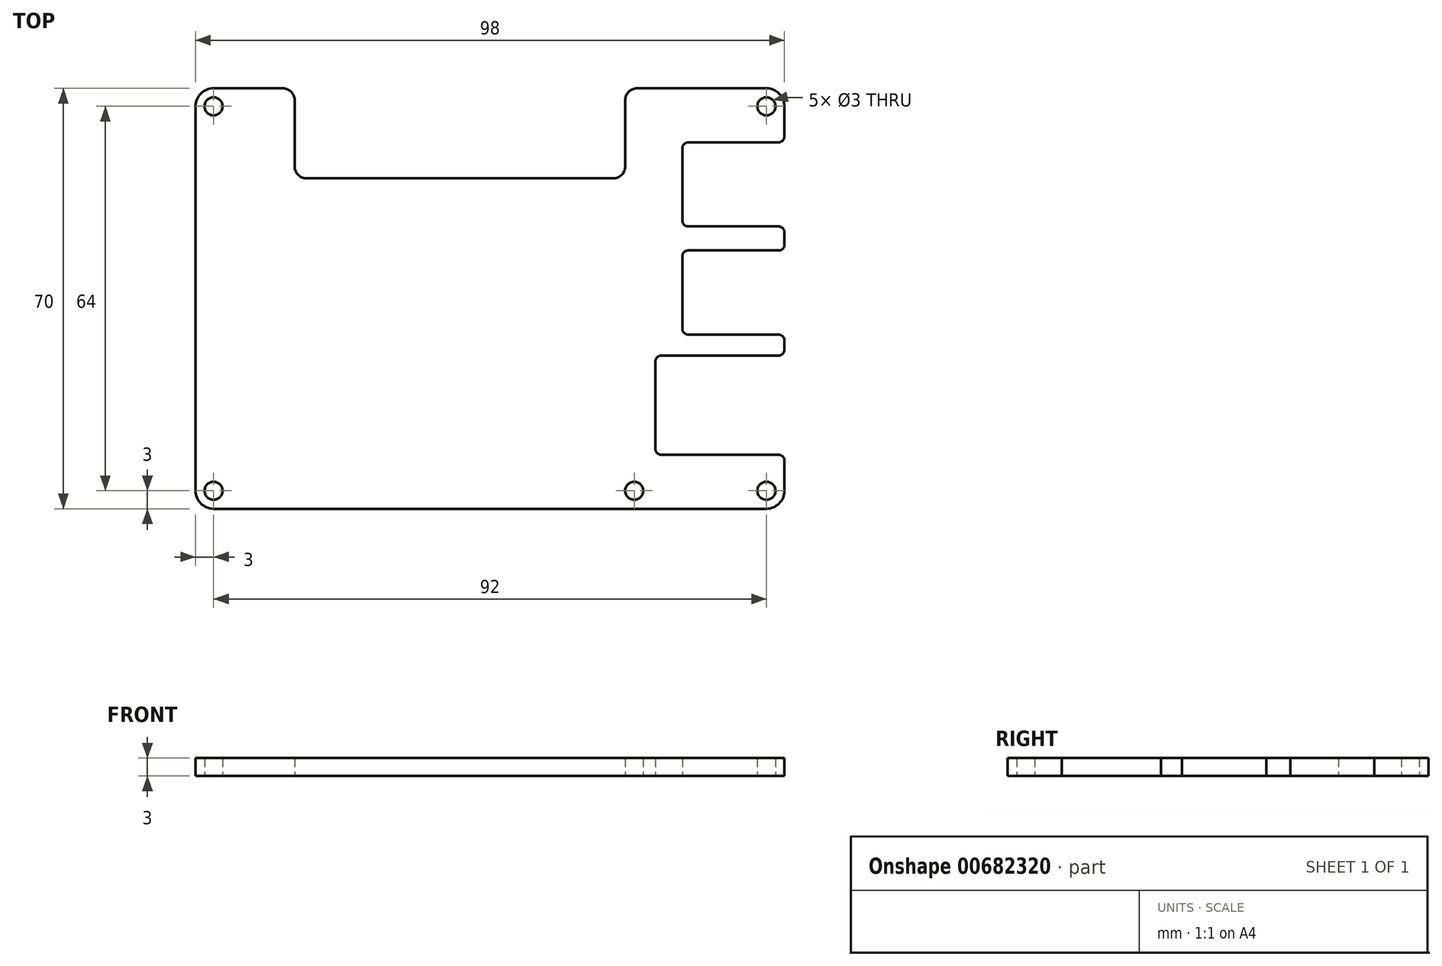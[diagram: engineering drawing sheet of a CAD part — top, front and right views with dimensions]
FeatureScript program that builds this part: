
annotation { "Feature Type Name" : "Feature", "Feature Type Description" : "" }
export const myFeature = defineFeature(function(context is Context, id is Id, definition is map)
    precondition{}
    {
        {
            var Q0;
            Q0=qCreatedBy(makeId("Top.planeOp"), FACE);
            var sketch = newSketch(context, id + "F0", { "sketchPlane" : qUnion([Q0])});
            skLineSegment(sketch, "E0.bottom", {"start": v(3, 0) * mm, "end": v(95, 0) * mm});
            skLineSegment(sketch, "E0.top", {"start": v(3, 70) * mm, "end": v(14.5, 70) * mm});
            skLineSegment(sketch, "E0.left", {"start": v(0, 3) * mm, "end": v(0, 67) * mm});
            skLineSegment(sketch, "E0.right", {"start": v(98, 3) * mm, "end": v(98, 8) * mm});
            skPoint(sketch, "E1.visualSharp", {"position": v(0, 70) * mm});
            skArc(sketch, "E1.filletArc", {"start": v(3, 70) * mm, "mid": v(0.88, 69.12) * mm, "end": v(0, 67) * mm});
            skPoint(sketch, "E2.visualSharp", {"position": v(98, 70) * mm});
            skArc(sketch, "E2.filletArc", {"start": v(98, 67) * mm, "mid": v(97.12, 69.12) * mm, "end": v(95, 70) * mm});
            skPoint(sketch, "E3.visualSharp", {"position": v(98, 0) * mm});
            skArc(sketch, "E3.filletArc", {"start": v(95, 0) * mm, "mid": v(97.12, 0.88) * mm, "end": v(98, 3) * mm});
            skPoint(sketch, "E4.visualSharp", {"position": v(0, 0) * mm});
            skArc(sketch, "E4.filletArc", {"start": v(0, 3) * mm, "mid": v(0.88, 0.88) * mm, "end": v(3, 0) * mm});
            skCircle(sketch, "E5", {"center": v(3, 67) * mm, "radius": 1.5 * mm});
            skCircle(sketch, "E6", {"center": v(95, 67) * mm, "radius": 1.5 * mm});
            skCircle(sketch, "E7", {"center": v(95, 3) * mm, "radius": 1.5 * mm});
            skCircle(sketch, "E8", {"center": v(3, 3) * mm, "radius": 1.5 * mm});
            skCircle(sketch, "E9", {"center": v(73, 3) * mm, "radius": 1.5 * mm});
            skLineSegment(sketch, "E10.bottom", {"start": v(97, 9) * mm, "end": v(77.5, 9) * mm});
            skLineSegment(sketch, "E10.top", {"start": v(97, 25.5) * mm, "end": v(77.5, 25.5) * mm});
            skLineSegment(sketch, "E10.right", {"start": v(76.5, 10) * mm, "end": v(76.5, 24.5) * mm});
            skLineSegment(sketch, "E11.bottom", {"start": v(97, 29) * mm, "end": v(82, 29) * mm});
            skLineSegment(sketch, "E11.top", {"start": v(97, 43) * mm, "end": v(82, 43) * mm});
            skLineSegment(sketch, "E11.right", {"start": v(81, 30) * mm, "end": v(81, 42) * mm});
            skLineSegment(sketch, "E12.bottom", {"start": v(97, 47) * mm, "end": v(82, 47) * mm});
            skLineSegment(sketch, "E12.top", {"start": v(97, 61) * mm, "end": v(82, 61) * mm});
            skLineSegment(sketch, "E12.right", {"start": v(81, 48) * mm, "end": v(81, 60) * mm});
            skPoint(sketch, "E13.visualSharp", {"position": v(81, 61) * mm});
            skArc(sketch, "E13.filletArc", {"start": v(82, 61) * mm, "mid": v(81.3, 60.7) * mm, "end": v(81, 60) * mm});
            skPoint(sketch, "E14.visualSharp", {"position": v(81, 47) * mm});
            skArc(sketch, "E14.filletArc", {"start": v(81, 48) * mm, "mid": v(81.3, 47.3) * mm, "end": v(82, 47) * mm});
            skPoint(sketch, "E15.visualSharp", {"position": v(81, 43) * mm});
            skArc(sketch, "E15.filletArc", {"start": v(82, 43) * mm, "mid": v(81.3, 42.7) * mm, "end": v(81, 42) * mm});
            skPoint(sketch, "E16.visualSharp", {"position": v(81, 29) * mm});
            skArc(sketch, "E16.filletArc", {"start": v(81, 30) * mm, "mid": v(81.3, 29.3) * mm, "end": v(82, 29) * mm});
            skPoint(sketch, "E17.visualSharp", {"position": v(76.5, 25.5) * mm});
            skArc(sketch, "E17.filletArc", {"start": v(77.5, 25.5) * mm, "mid": v(76.8, 25.2) * mm, "end": v(76.5, 24.5) * mm});
            skPoint(sketch, "E18.visualSharp", {"position": v(76.5, 9) * mm});
            skArc(sketch, "E18.filletArc", {"start": v(76.5, 10) * mm, "mid": v(76.8, 9.3) * mm, "end": v(77.5, 9) * mm});
            skLineSegment(sketch, "E19.trimOffspring", {"start": v(98, 44) * mm, "end": v(98, 46) * mm});
            skLineSegment(sketch, "E20.trimOffspring", {"start": v(98, 26.5) * mm, "end": v(98, 28) * mm});
            skLineSegment(sketch, "E21.trimOffspring", {"start": v(98, 62) * mm, "end": v(98, 67) * mm});
            skPoint(sketch, "E22.visualSharp", {"position": v(98, 47) * mm});
            skArc(sketch, "E22.filletArc", {"start": v(98, 46) * mm, "mid": v(97.7, 46.7) * mm, "end": v(97, 47) * mm});
            skPoint(sketch, "E23.visualSharp", {"position": v(98, 43) * mm});
            skArc(sketch, "E23.filletArc", {"start": v(97, 43) * mm, "mid": v(97.7, 43.3) * mm, "end": v(98, 44) * mm});
            skPoint(sketch, "E24.visualSharp", {"position": v(98, 61) * mm});
            skArc(sketch, "E24.filletArc", {"start": v(97, 61) * mm, "mid": v(97.7, 61.3) * mm, "end": v(98, 62) * mm});
            skPoint(sketch, "E25.visualSharp", {"position": v(98, 29) * mm});
            skArc(sketch, "E25.filletArc", {"start": v(98, 28) * mm, "mid": v(97.7, 28.7) * mm, "end": v(97, 29) * mm});
            skPoint(sketch, "E26.visualSharp", {"position": v(98, 25.5) * mm});
            skArc(sketch, "E26.filletArc", {"start": v(97, 25.5) * mm, "mid": v(97.7, 25.8) * mm, "end": v(98, 26.5) * mm});
            skPoint(sketch, "E27.visualSharp", {"position": v(98, 9) * mm});
            skArc(sketch, "E27.filletArc", {"start": v(98, 8) * mm, "mid": v(97.7, 8.7) * mm, "end": v(97, 9) * mm});
            skPoint(sketch, "E28", {"position": v(81, 36) * mm});
            skPoint(sketch, "E29", {"position": v(81, 54) * mm});
            skPoint(sketch, "E30", {"position": v(76.5, 17.25) * mm});
            skLineSegment(sketch, "E31", {"start": v(16.5, 68) * mm, "end": v(16.5, 57) * mm});
            skLineSegment(sketch, "E32", {"start": v(18.5, 55) * mm, "end": v(69.5, 55) * mm});
            skLineSegment(sketch, "E33", {"start": v(71.5, 57) * mm, "end": v(71.5, 68) * mm});
            skLineSegment(sketch, "E34.trimOffspring", {"start": v(73.5, 70) * mm, "end": v(95, 70) * mm});
            skPoint(sketch, "E35.visualSharp", {"position": v(16.5, 70) * mm});
            skArc(sketch, "E35.filletArc", {"start": v(16.5, 68) * mm, "mid": v(15.91, 69.41) * mm, "end": v(14.5, 70) * mm});
            skPoint(sketch, "E36.visualSharp", {"position": v(16.5, 55) * mm});
            skArc(sketch, "E36.filletArc", {"start": v(16.5, 57) * mm, "mid": v(17.09, 55.59) * mm, "end": v(18.5, 55) * mm});
            skPoint(sketch, "E37.visualSharp", {"position": v(71.5, 55) * mm});
            skArc(sketch, "E37.filletArc", {"start": v(69.5, 55) * mm, "mid": v(70.91, 55.59) * mm, "end": v(71.5, 57) * mm});
            skPoint(sketch, "E38.visualSharp", {"position": v(71.5, 70) * mm});
            skArc(sketch, "E38.filletArc", {"start": v(73.5, 70) * mm, "mid": v(72.09, 69.41) * mm, "end": v(71.5, 68) * mm});
            skSolve(sketch);
        }
        {
            var Q0;
            Q0 = qSketchRegion(id + "F0", true);
            extrude(context, id + "F1", {"entities" : qUnion([Q0]), "depth" : 3 * mm, "offsetDistance" : 25 * mm});
        }
    });
